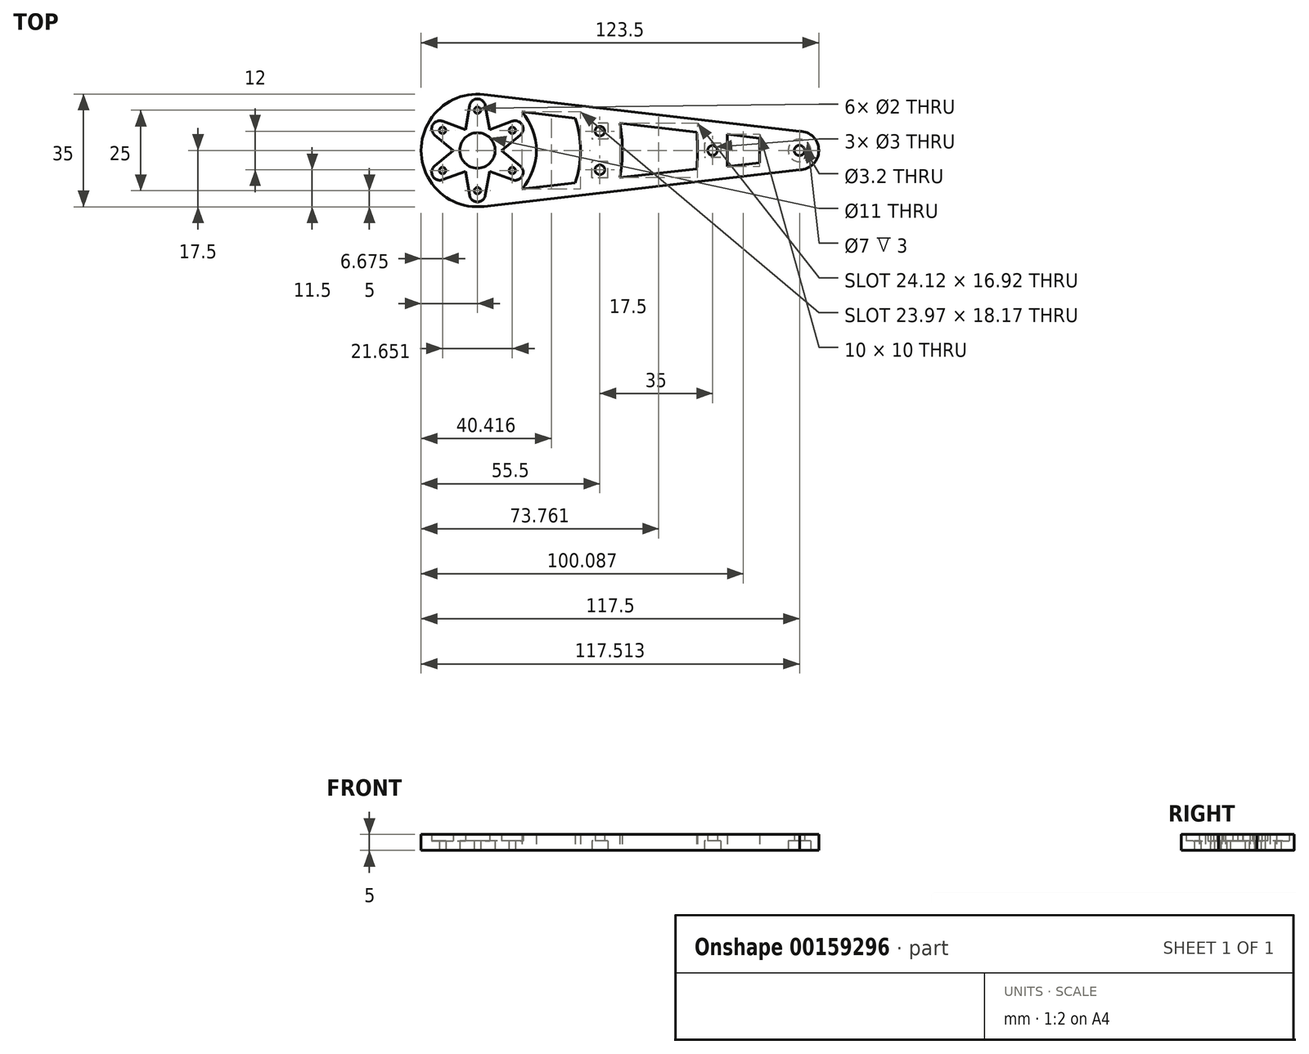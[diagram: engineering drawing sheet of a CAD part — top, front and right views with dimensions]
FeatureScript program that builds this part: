
annotation { "Feature Type Name" : "Feature", "Feature Type Description" : "" }
export const myFeature = defineFeature(function(context is Context, id is Id, definition is map)
    precondition{}
    {
        {
            var Q0;
            Q0=qCreatedBy(makeId("Top.planeOp"),FACE);
            var sketch = newSketch(context, id + "F0", { "sketchPlane" : qUnion([Q0])});
            skArc(sketch, "E0", {"start": v(2.02, 17.38) * mm, "mid": v(-17.5, 0) * mm, "end": v(2.02, -17.38) * mm});
            skArc(sketch, "E1", {"start": v(100.03, -6) * mm, "mid": v(106, 0) * mm, "end": v(100.03, 6) * mm});
            skLineSegment(sketch, "E2", {"start": v(100.03, 6) * mm, "end": v(2.02, 17.38) * mm});
            skLineSegment(sketch, "E3", {"start": v(100.03, -6) * mm, "end": v(2.02, -17.38) * mm});
            skArc(sketch, "E4", {"start": v(2.46, 13.93) * mm, "mid": v(0, 16) * mm, "end": v(-2.46, 13.93) * mm});
            skArc(sketch, "E5.1.0", {"start": v(-10.83, 9.1) * mm, "mid": v(-13.86, 8) * mm, "end": v(-13.3, 4.83) * mm});
            skArc(sketch, "E5.2.0", {"start": v(-13.3, -4.83) * mm, "mid": v(-13.86, -8) * mm, "end": v(-10.83, -9.1) * mm});
            skArc(sketch, "E5.3.0", {"start": v(-2.46, -13.93) * mm, "mid": v(0, -16) * mm, "end": v(2.46, -13.93) * mm});
            skArc(sketch, "E5.4.0", {"start": v(10.83, -9.1) * mm, "mid": v(13.86, -8) * mm, "end": v(13.3, -4.83) * mm});
            skArc(sketch, "E5.5.0", {"start": v(13.3, 4.83) * mm, "mid": v(13.86, 8) * mm, "end": v(10.83, 9.1) * mm});
            skPoint(sketch, "E6", {"position": v(7.5, 0) * mm});
            skPoint(sketch, "E7.1.0", {"position": v(3.75, 6.5) * mm});
            skPoint(sketch, "E7.2.0", {"position": v(-3.75, 6.5) * mm});
            skPoint(sketch, "E7.3.0", {"position": v(-7.5, 0) * mm});
            skPoint(sketch, "E7.4.0", {"position": v(-3.75, -6.5) * mm});
            skPoint(sketch, "E7.5.0", {"position": v(3.75, -6.5) * mm});
            skLineSegment(sketch, "E8", {"start": v(3.75, 6.5) * mm, "end": v(2.46, 13.93) * mm});
            skLineSegment(sketch, "E9", {"start": v(3.75, 6.5) * mm, "end": v(10.83, 9.1) * mm});
            skLineSegment(sketch, "E10", {"start": v(7.5, 0) * mm, "end": v(13.3, 4.83) * mm});
            skLineSegment(sketch, "E11", {"start": v(7.5, 0) * mm, "end": v(13.3, -4.83) * mm});
            skLineSegment(sketch, "E12", {"start": v(3.75, -6.5) * mm, "end": v(10.83, -9.1) * mm});
            skLineSegment(sketch, "E13", {"start": v(3.75, -6.5) * mm, "end": v(2.46, -13.93) * mm});
            skLineSegment(sketch, "E14", {"start": v(-3.75, -6.5) * mm, "end": v(-2.46, -13.93) * mm});
            skLineSegment(sketch, "E15", {"start": v(-3.75, -6.5) * mm, "end": v(-10.83, -9.1) * mm});
            skLineSegment(sketch, "E16", {"start": v(-7.5, 0) * mm, "end": v(-13.3, -4.83) * mm});
            skLineSegment(sketch, "E17", {"start": v(-7.5, 0) * mm, "end": v(-13.3, 4.83) * mm});
            skLineSegment(sketch, "E18", {"start": v(-3.75, 6.5) * mm, "end": v(-10.83, 9.1) * mm});
            skLineSegment(sketch, "E19", {"start": v(-3.75, 6.5) * mm, "end": v(-2.46, 13.93) * mm});
            skCircle(sketch, "E20", {"center": v(0, 0) * mm, "radius": 5.5 * mm});
            skArc(sketch, "E21", {"start": v(44.2, -8.46) * mm, "mid": v(45, 0) * mm, "end": v(44.2, 8.46) * mm});
            skArc(sketch, "E22", {"start": v(68.09, -5.68) * mm, "mid": v(68.32, 0) * mm, "end": v(68.09, 5.68) * mm});
            skLineSegment(sketch, "E23", {"start": v(44.2, -8.46) * mm, "end": v(68.09, -5.68) * mm});
            skLineSegment(sketch, "E24", {"start": v(68.09, 5.68) * mm, "end": v(44.2, 8.46) * mm});
            skLineSegment(sketch, "E25", {"start": v(77.59, 5) * mm, "end": v(77.59, -5) * mm});
            skLineSegment(sketch, "E26", {"start": v(87.59, 3.84) * mm, "end": v(87.59, -3.84) * mm});
            skLineSegment(sketch, "E27", {"start": v(77.59, 5) * mm, "end": v(87.59, 3.84) * mm});
            skLineSegment(sketch, "E28", {"start": v(77.59, -5) * mm, "end": v(87.59, -3.84) * mm});
            skArc(sketch, "E29", {"start": v(13.83, -11.98) * mm, "mid": v(18.3, 0) * mm, "end": v(13.83, 11.98) * mm});
            skArc(sketch, "E30", {"start": v(30.38, -10.06) * mm, "mid": v(32, 0) * mm, "end": v(30.38, 10.06) * mm});
            skLineSegment(sketch, "E31", {"start": v(13.83, 11.98) * mm, "end": v(30.38, 10.06) * mm});
            skLineSegment(sketch, "E32", {"start": v(13.83, -11.98) * mm, "end": v(30.38, -10.06) * mm});
            skCircle(sketch, "E33", {"center": v(100, 0) * mm, "radius": 1.6 * mm});
            skSolve(sketch);
        }
        {
            var Q0;
            Q0=makeQuery(id+"F0.imprint","IMPRINT",FACE,{"disambiguationData":[TD([[makeQuery(id+"F0.imprint","IMPRINT",EDGE,{"derivedFrom":sQuery(id+"F0.wireOp",EDGE,"E0")}),1.0]])]});
            var Q1;
            Q1=makeQuery(id+"F0.imprint","IMPRINT",FACE,{"disambiguationData":[TD([[makeQuery(id+"F0.imprint","IMPRINT",EDGE,{"derivedFrom":sQuery(id+"F0.wireOp",EDGE,"E4")}),1.0]])]});
            extrude(context, id + "F1", {"entities" : qUnion([Q0, Q1]), "depth" : 3 * mm});
        }
        {
            var Q0;
            Q0=makeQuery(id+"F0.imprint","IMPRINT",FACE,{"disambiguationData":[TD([[makeQuery(id+"F0.imprint","IMPRINT",EDGE,{"derivedFrom":sQuery(id+"F0.wireOp",EDGE,"E0")}),1.0]])]});
            var Q1;
            Q1=makeQuery(id+"F0.imprint","IMPRINT",FACE,{"disambiguationData":[TD([[makeQuery(id+"F0.imprint","IMPRINT",EDGE,{"derivedFrom":sQuery(id+"F0.wireOp",EDGE,"ZcYsQESy-AeiV-42ZS-168l-Z5ThC9YDKqhQ.bottom")}),-1.0]])]});
            extrude(context, id + "F2", {"entities" : qUnion([Q0, Q1]), "operationType" : NewBodyOperationType.ADD, "depth" : 5 * mm});
        }
        {
            var Q0;
            Q0=makeQuery(id+"F0.imprint","IMPRINT",FACE,{"disambiguationData":[TD([[makeQuery(id+"F0.imprint","IMPRINT",EDGE,{"derivedFrom":sQuery(id+"F0.wireOp",EDGE,"E0")}),1.0]])]});
            var sketch = newSketch(context, id + "F3", { "sketchPlane" : qUnion([Q0])});
            skCircle(sketch, "E34", {"center": v(0, -12.5) * mm, "radius": 1 * mm});
            skCircle(sketch, "E35.1.0", {"center": v(10.83, -6.25) * mm, "radius": 1 * mm});
            skCircle(sketch, "E35.2.0", {"center": v(10.83, 6.25) * mm, "radius": 1 * mm});
            skCircle(sketch, "E35.3.0", {"center": v(0, 12.5) * mm, "radius": 1 * mm});
            skCircle(sketch, "E35.4.0", {"center": v(-10.83, 6.25) * mm, "radius": 1 * mm});
            skCircle(sketch, "E35.5.0", {"center": v(-10.83, -6.25) * mm, "radius": 1 * mm});
            skPoint(sketch, "E35.center", {"position": v(0, 0) * mm});
            skLineSegment(sketch, "E36.bottom", {"start": v(40.5, 8.5) * mm, "end": v(35.5, 8.5) * mm});
            skLineSegment(sketch, "E36.top", {"start": v(40.5, 3.5) * mm, "end": v(35.5, 3.5) * mm});
            skLineSegment(sketch, "E36.left", {"start": v(40.5, 8.5) * mm, "end": v(40.5, 3.5) * mm});
            skLineSegment(sketch, "E36.right", {"start": v(35.5, 8.5) * mm, "end": v(35.5, 3.5) * mm});
            skPoint(sketch, "E36.middle", {"position": v(38, 6) * mm});
            skLineSegment(sketch, "E37.bottom", {"start": v(75.5, 2.25) * mm, "end": v(70.5, 2.25) * mm});
            skLineSegment(sketch, "E37.top", {"start": v(75.5, -2.25) * mm, "end": v(70.5, -2.25) * mm});
            skLineSegment(sketch, "E37.left", {"start": v(75.5, 2.25) * mm, "end": v(75.5, -2.25) * mm});
            skLineSegment(sketch, "E37.right", {"start": v(70.5, 2.25) * mm, "end": v(70.5, -2.25) * mm});
            skPoint(sketch, "E37.middle", {"position": v(73, 0) * mm});
            skLineSegment(sketch, "E38.bottom", {"start": v(40.5, -8.5) * mm, "end": v(35.5, -8.5) * mm});
            skLineSegment(sketch, "E38.top", {"start": v(40.5, -3.5) * mm, "end": v(35.5, -3.5) * mm});
            skLineSegment(sketch, "E38.left", {"start": v(40.5, -8.5) * mm, "end": v(40.5, -3.5) * mm});
            skLineSegment(sketch, "E38.right", {"start": v(35.5, -8.5) * mm, "end": v(35.5, -3.5) * mm});
            skPoint(sketch, "E38.middle", {"position": v(38, -6) * mm});
            skCircle(sketch, "E39", {"center": v(100.01, 0) * mm, "radius": 3.5 * mm});
            skSolve(sketch);
        }
        {
            var Q0;
            Q0 = qSketchRegion(id + "F3", true);
            extrude(context, id + "F4", {"entities" : qUnion([Q0]), "operationType" : NewBodyOperationType.REMOVE, "depth" : 3 * mm});
        }
        {
            var Q0;
            Q0=makeQuery(id+"F0.imprint","IMPRINT",FACE,{"disambiguationData":[TD([[makeQuery(id+"F0.imprint","IMPRINT",EDGE,{"derivedFrom":sQuery(id+"F0.wireOp",EDGE,"E0")}),1.0]])]});
            var sketch = newSketch(context, id + "F5", { "sketchPlane" : qUnion([Q0])});
            skCircle(sketch, "E40", {"center": v(38, -6) * mm, "radius": 1.5 * mm});
            skCircle(sketch, "E41", {"center": v(73, 0) * mm, "radius": 1.5 * mm});
            skCircle(sketch, "E42", {"center": v(38, 6) * mm, "radius": 1.5 * mm});
            skSolve(sketch);
        }
        {
            var Q0;
            Q0 = qSketchRegion(id + "F5", true);
            extrude(context, id + "F6", {"entities" : qUnion([Q0]), "operationType" : NewBodyOperationType.REMOVE, "depth" : 25 * mm});
        }
        {
            var Q0;
            Q0=makeQuery(id+"F3.imprint","IMPRINT",FACE,{"disambiguationData":[TD([[makeQuery(id+"F3.imprint","IMPRINT",EDGE,{"derivedFrom":sQuery(id+"F3.wireOp",EDGE,"E34")}),1.0]])]});
            var Q1;
            Q1=makeQuery(id+"F3.imprint","IMPRINT",FACE,{"disambiguationData":[TD([[makeQuery(id+"F3.imprint","IMPRINT",EDGE,{"derivedFrom":sQuery(id+"F3.wireOp",EDGE,"E35.1.0")}),1.0]])]});
            var Q2;
            Q2=makeQuery(id+"F3.imprint","IMPRINT",FACE,{"disambiguationData":[TD([[makeQuery(id+"F3.imprint","IMPRINT",EDGE,{"derivedFrom":sQuery(id+"F3.wireOp",EDGE,"E35.2.0")}),1.0]])]});
            var Q3;
            Q3=makeQuery(id+"F3.imprint","IMPRINT",FACE,{"disambiguationData":[TD([[makeQuery(id+"F3.imprint","IMPRINT",EDGE,{"derivedFrom":sQuery(id+"F3.wireOp",EDGE,"E35.3.0")}),1.0]])]});
            var Q4;
            Q4=makeQuery(id+"F3.imprint","IMPRINT",FACE,{"disambiguationData":[TD([[makeQuery(id+"F3.imprint","IMPRINT",EDGE,{"derivedFrom":sQuery(id+"F3.wireOp",EDGE,"E35.4.0")}),1.0]])]});
            var Q5;
            Q5=makeQuery(id+"F3.imprint","IMPRINT",FACE,{"disambiguationData":[TD([[makeQuery(id+"F3.imprint","IMPRINT",EDGE,{"derivedFrom":sQuery(id+"F3.wireOp",EDGE,"E35.5.0")}),1.0]])]});
            var Q6;
            {var subQ0=sQuery(id+"F3.wireOp",EDGE,"E37.left");var subQ1=sQuery(id+"F3.wireOp",EDGE,"E37.bottom");var subQ2=makeQuery(id+"F3.imprint","INTERSECT",VERTEX,{"derivedFrom":[subQ1,subQ0]});Q6=makeQuery(id+"F3.imprint","IMPRINT",FACE,{"disambiguationData":[TD([[makeQuery(id+"F3.imprint","IMPRINT",EDGE,{"disambiguationData":[TD([[subQ2,-1.0]])],"derivedFrom":subQ1}),1.0]])]});}
            extrude(context, id + "F7", {"entities" : qUnion([Q0, Q1, Q2, Q3, Q4, Q5, Q6]), "operationType" : NewBodyOperationType.REMOVE, "oppositeDirection" : true, "depth" : 25 * mm});
        }
    });
